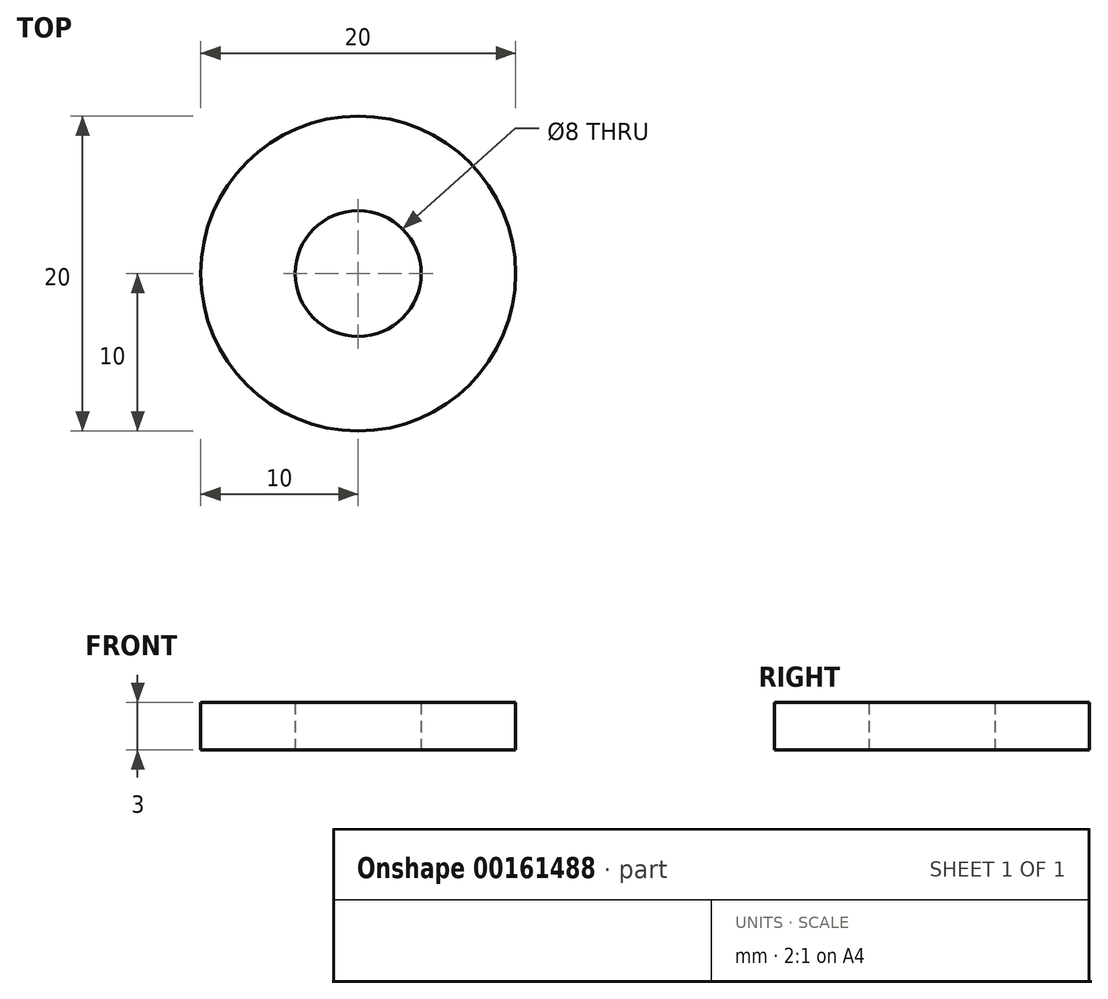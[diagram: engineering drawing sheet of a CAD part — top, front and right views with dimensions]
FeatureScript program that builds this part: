
annotation { "Feature Type Name" : "Feature", "Feature Type Description" : "" }
export const myFeature = defineFeature(function(context is Context, id is Id, definition is map)
    precondition{}
    {
        {
            var Q0;
            Q0=qCreatedBy(makeId("Top.planeOp"),FACE);
            var sketch = newSketch(context, id + "F0", { "sketchPlane" : qUnion([Q0])});
            skCircle(sketch, "E0", {"center": v(0, 0) * mm, "radius": 4 * mm});
            skCircle(sketch, "E1", {"center": v(0, 0) * mm, "radius": 10 * mm});
            skSolve(sketch);
        }
        {
            var Q0;
            Q0 = qSketchRegion(id + "F0", true);
            extrude(context, id + "F1", {"entities" : qUnion([Q0]), "depth" : 3 * mm});
        }
    });
